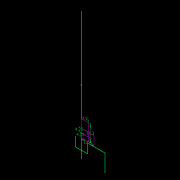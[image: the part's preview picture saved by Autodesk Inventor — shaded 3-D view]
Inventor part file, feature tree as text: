
AUTODESK INVENTOR PART (.ipt)
format: ipt  version: 2016 (Build 200138000, 138)  size: 673,280 bytes
history: native  units: mm
features: sketch x2
ambient origin geometry x8: Origin, YZ Plane, XZ Plane, XY Plane, X Axis, Y Axis, Z Axis, Center Point
feature tree (2):
  sketch  "Sketch1"  dims[d2=13.4mm]
  sketch  "Sketch2"  dims[d3=8.6mm d4=17.4mm d5=7.6mm d6=0.5mm d7=1.0mm d10=5.0mm d11=5.0mm d12=0.5mm d15=2.0mm d16=4.0mm d17=4.0mm d18=4.25mm d19=4.25mm d20=13.4mm d21=7.5mm d22=17.3mm]
